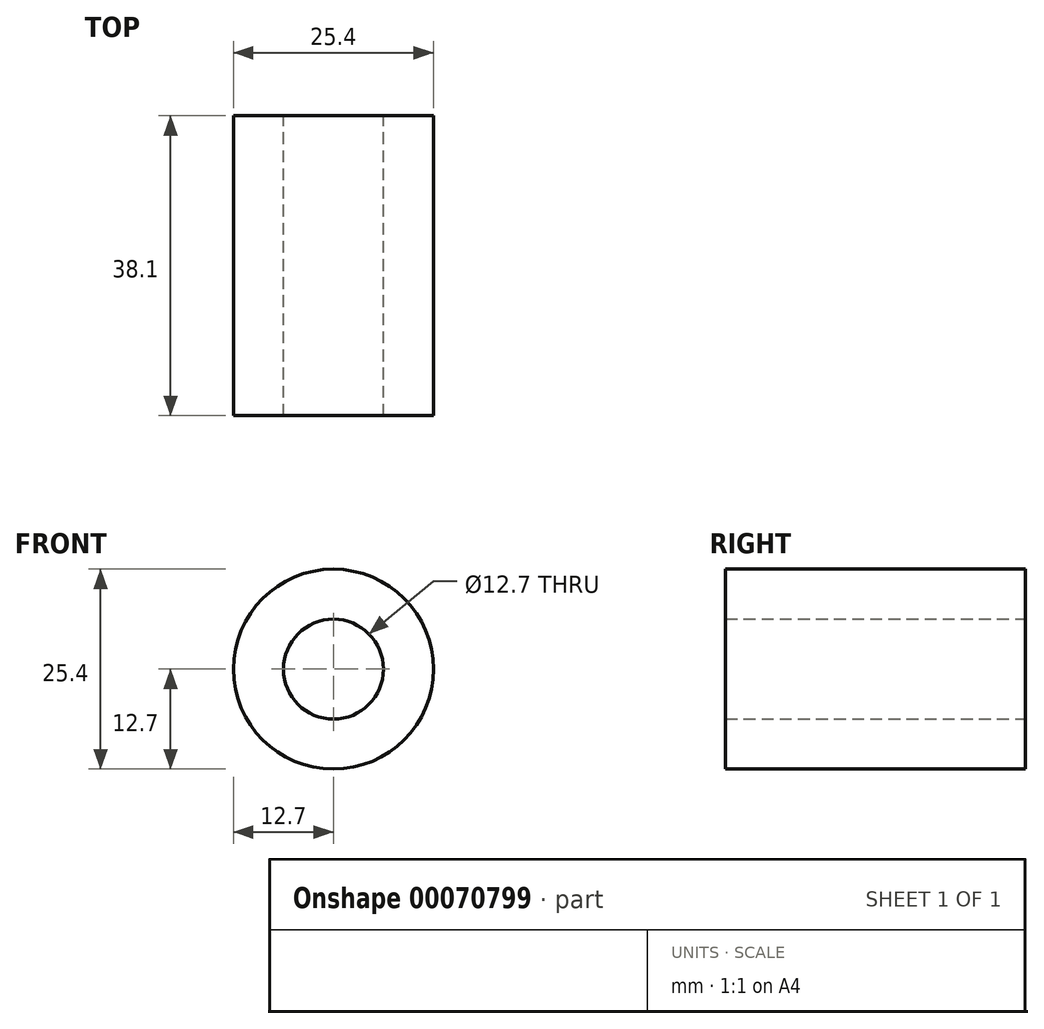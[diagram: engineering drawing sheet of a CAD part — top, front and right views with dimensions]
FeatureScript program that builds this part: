
annotation { "Feature Type Name" : "Feature", "Feature Type Description" : "" }
export const myFeature = defineFeature(function(context is Context, id is Id, definition is map)
    precondition{}
    {
        {
            var Q0;
            Q0=qCreatedBy(makeId("Front.planeOp"),FACE);
            var sketch = newSketch(context, id + "F0", { "sketchPlane" : qUnion([Q0])});
            skCircle(sketch, "E0", {"center": v(0, 0) * mm, "radius": 12.7 * mm});
            skCircle(sketch, "E1", {"center": v(0, 0) * mm, "radius": 6.35 * mm});
            skSolve(sketch);
        }
        {
            var Q0;
            Q0=makeQuery(id+"F0.imprint","IMPRINT",FACE,{"disambiguationData":[TD([[makeQuery(id+"F0.imprint","IMPRINT",EDGE,{"derivedFrom":sQuery(id+"F0.wireOp",EDGE,"E0")}),1.0]])]});
            extrude(context, id + "F1", {"entities" : qUnion([Q0]), "depth" : 38.1 * mm});
        }
    });
